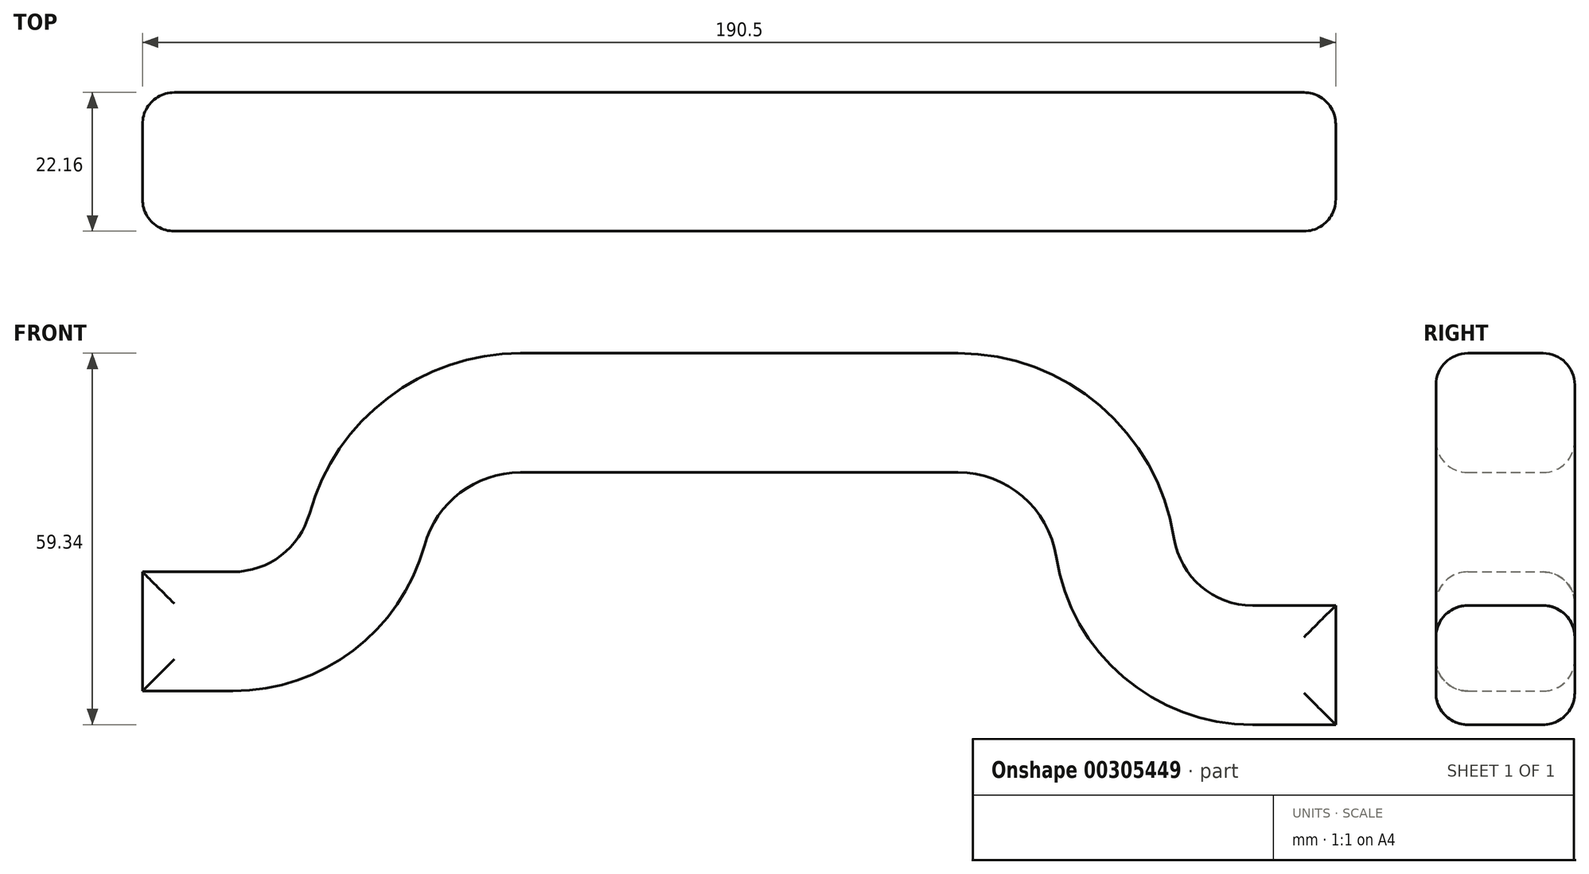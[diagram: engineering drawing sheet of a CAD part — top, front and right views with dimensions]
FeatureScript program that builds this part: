
annotation { "Feature Type Name" : "Feature", "Feature Type Description" : "" }
export const myFeature = defineFeature(function(context is Context, id is Id, definition is map)
    precondition{}
    {
        {
            var Q0;
            Q0=qCreatedBy(makeId("Front.planeOp"),FACE);
            var sketch = newSketch(context, id + "F0", { "sketchPlane" : qUnion([Q0])});
            skLineSegment(sketch, "E0.top", {"start": v(-41.23, 72.15) * mm, "end": v(28.62, 72.15) * mm});
            skLineSegment(sketch, "E0.left", {"start": v(-101.55, 18.18) * mm, "end": v(-101.55, 37.23) * mm});
            skLineSegment(sketch, "E0.right", {"start": v(88.95, 12.8) * mm, "end": v(88.95, 31.86) * mm});
            skLineSegment(sketch, "E1.bottom", {"start": v(-41.23, 53.1) * mm, "end": v(28.62, 53.1) * mm});
            skLineSegment(sketch, "E1.top", {"start": v(-6.3, 21.35) * mm, "end": v(28.62, 21.35) * mm});
            skLineSegment(sketch, "E2", {"start": v(-6.3, 72.15) * mm, "end": v(-6.3, 21.35) * mm, "construction": true});
            skLineSegment(sketch, "E3", {"start": v(-57.1, 37.23) * mm, "end": v(-41.23, 37.23) * mm, "construction": true});
            skLineSegment(sketch, "E4", {"start": v(-41.23, 53.1) * mm, "end": v(-41.23, 21.35) * mm, "construction": true});
            skLineSegment(sketch, "E5", {"start": v(28.62, 53.1) * mm, "end": v(28.62, 21.35) * mm, "construction": true});
            skArc(sketch, "E6", {"start": v(-41.23, 53.1) * mm, "mid": v(-52.45, 48.45) * mm, "end": v(-57.1, 37.23) * mm});
            skArc(sketch, "E7", {"start": v(44.5, 37.23) * mm, "mid": v(39.85, 48.45) * mm, "end": v(28.62, 53.1) * mm});
            skPoint(sketch, "E8.orphan", {"position": v(-57.1, 53.1) * mm});
            skPoint(sketch, "E9.orphan", {"position": v(-57.1, 21.35) * mm});
            skPoint(sketch, "E10.orphan", {"position": v(44.5, 21.35) * mm});
            skPoint(sketch, "E11.orphan", {"position": v(44.5, 53.1) * mm});
            skArc(sketch, "E12.trimOffspring", {"start": v(-41.23, 72.15) * mm, "mid": v(-62.38, 65.02) * mm, "end": v(-74.89, 46.54) * mm});
            skPoint(sketch, "E13.orphan", {"position": v(88.95, 72.15) * mm});
            skPoint(sketch, "E14.orphan", {"position": v(-101.55, 72.15) * mm});
            skLineSegment(sketch, "E15", {"start": v(92.12, 53.1) * mm, "end": v(-107.75, 53.1) * mm, "construction": true});
            skLineSegment(sketch, "E16", {"start": v(-101.55, 37.23) * mm, "end": v(-87.13, 37.23) * mm});
            skArc(sketch, "E17", {"start": v(63.13, 42.6) * mm, "mid": v(51.34, 63.76) * mm, "end": v(28.62, 72.15) * mm});
            skLineSegment(sketch, "E18", {"start": v(88.95, 31.86) * mm, "end": v(75.68, 31.86) * mm});
            skPoint(sketch, "E19.visualSharp", {"position": v(-76.15, 37.23) * mm});
            skArc(sketch, "E19.filletArc", {"start": v(-87.13, 37.23) * mm, "mid": v(-79.44, 39.82) * mm, "end": v(-74.89, 46.54) * mm});
            skPoint(sketch, "E20.visualSharp", {"position": v(63.13, 31.86) * mm});
            skArc(sketch, "E20.filletArc", {"start": v(63.13, 42.6) * mm, "mid": v(67.42, 34.9) * mm, "end": v(75.68, 31.86) * mm});
            skLineSegment(sketch, "E21.0", {"start": v(88.95, 12.8) * mm, "end": v(75.68, 12.8) * mm});
            skArc(sketch, "E21.1", {"start": v(44.3, 39.67) * mm, "mid": v(55.03, 20.44) * mm, "end": v(75.68, 12.8) * mm});
            skArc(sketch, "E21.2", {"start": v(44.3, 39.67) * mm, "mid": v(38.95, 49.29) * mm, "end": v(28.62, 53.1) * mm});
            skLineSegment(sketch, "E21.3", {"start": v(-101.55, 18.18) * mm, "end": v(-87.13, 18.18) * mm});
            skArc(sketch, "E21.4", {"start": v(-87.13, 18.18) * mm, "mid": v(-67.9, 24.66) * mm, "end": v(-56.53, 41.46) * mm});
            skArc(sketch, "E21.5", {"start": v(-41.23, 53.1) * mm, "mid": v(-50.84, 49.86) * mm, "end": v(-56.53, 41.46) * mm});
            skPoint(sketch, "E22.orphan", {"position": v(-101.55, -19.92) * mm});
            skPoint(sketch, "E0.bottom.end.orphan", {"position": v(88.95, -19.92) * mm});
            skPoint(sketch, "E23.orphan", {"position": v(-6.3, -19.92) * mm});
            skLineSegment(sketch, "E24.trimOffspring", {"start": v(28.62, 37.23) * mm, "end": v(44.5, 37.23) * mm, "construction": true});
            skSolve(sketch);
        }
        {
            var Q0;
            Q0=makeQuery(id+"F0.imprint","IMPRINT",FACE,{"disambiguationData":[TD([[makeQuery(id+"F0.imprint","IMPRINT",EDGE,{"derivedFrom":sQuery(id+"F0.wireOp",EDGE,"E0.bottom")}),1.0]])]});
            var Q1;
            Q1=makeQuery(id+"F0.imprint","IMPRINT",FACE,{"disambiguationData":[TD([[makeQuery(id+"F0.imprint","IMPRINT",EDGE,{"derivedFrom":sQuery(id+"F0.wireOp",EDGE,"E0.top")}),-1.0]])]});
            extrude(context, id + "F1", {"entities" : qUnion([Q0, Q1]), "depth" : 22.16 * mm});
        }
        {
            var Q0;
            Q0=makeQuery(id+"F1.opExtrude","CAP_FACE",FACE,{"disambiguationData":[OSD([sQuery(id+"F0.wireOp",EDGE,"E0.top"),sQuery(id+"F0.wireOp",EDGE,"E0.left"),sQuery(id+"F0.wireOp",EDGE,"E0.right"),sQuery(id+"F0.wireOp",EDGE,"E12.trimOffspring"),sQuery(id+"F0.wireOp",EDGE,"E16"),sQuery(id+"F0.wireOp",EDGE,"E17"),sQuery(id+"F0.wireOp",EDGE,"E18"),sQuery(id+"F0.wireOp",EDGE,"E19.filletArc"),sQuery(id+"F0.wireOp",EDGE,"E20.filletArc"),sQuery(id+"F0.wireOp",EDGE,"E21.0"),sQuery(id+"F0.wireOp",EDGE,"E21.1"),sQuery(id+"F0.wireOp",EDGE,"E21.2"),sQuery(id+"F0.wireOp",EDGE,"E21.3"),sQuery(id+"F0.wireOp",EDGE,"E21.4"),sQuery(id+"F0.wireOp",EDGE,"E21.5"),sQuery(id+"F0.wireOp",EDGE,"E1.bottom")])],"isStart":false});
            var Q1;
            Q1=makeQuery(id+"F1.opExtrude","CAP_FACE",FACE,{"disambiguationData":[OSD([sQuery(id+"F0.wireOp",EDGE,"E0.top"),sQuery(id+"F0.wireOp",EDGE,"E0.left"),sQuery(id+"F0.wireOp",EDGE,"E0.right"),sQuery(id+"F0.wireOp",EDGE,"E12.trimOffspring"),sQuery(id+"F0.wireOp",EDGE,"E16"),sQuery(id+"F0.wireOp",EDGE,"E17"),sQuery(id+"F0.wireOp",EDGE,"E18"),sQuery(id+"F0.wireOp",EDGE,"E19.filletArc"),sQuery(id+"F0.wireOp",EDGE,"E20.filletArc"),sQuery(id+"F0.wireOp",EDGE,"E21.0"),sQuery(id+"F0.wireOp",EDGE,"E21.1"),sQuery(id+"F0.wireOp",EDGE,"E21.2"),sQuery(id+"F0.wireOp",EDGE,"E21.3"),sQuery(id+"F0.wireOp",EDGE,"E21.4"),sQuery(id+"F0.wireOp",EDGE,"E21.5"),sQuery(id+"F0.wireOp",EDGE,"E1.bottom")])],"isStart":true});
            fillet(context, id + "F2", {"entities" : qUnion([Q0, Q1]), "radius" : 5.08 * mm, "tangentPropagation" : true, "allowEdgeOverflow" : false});
        }
    });
